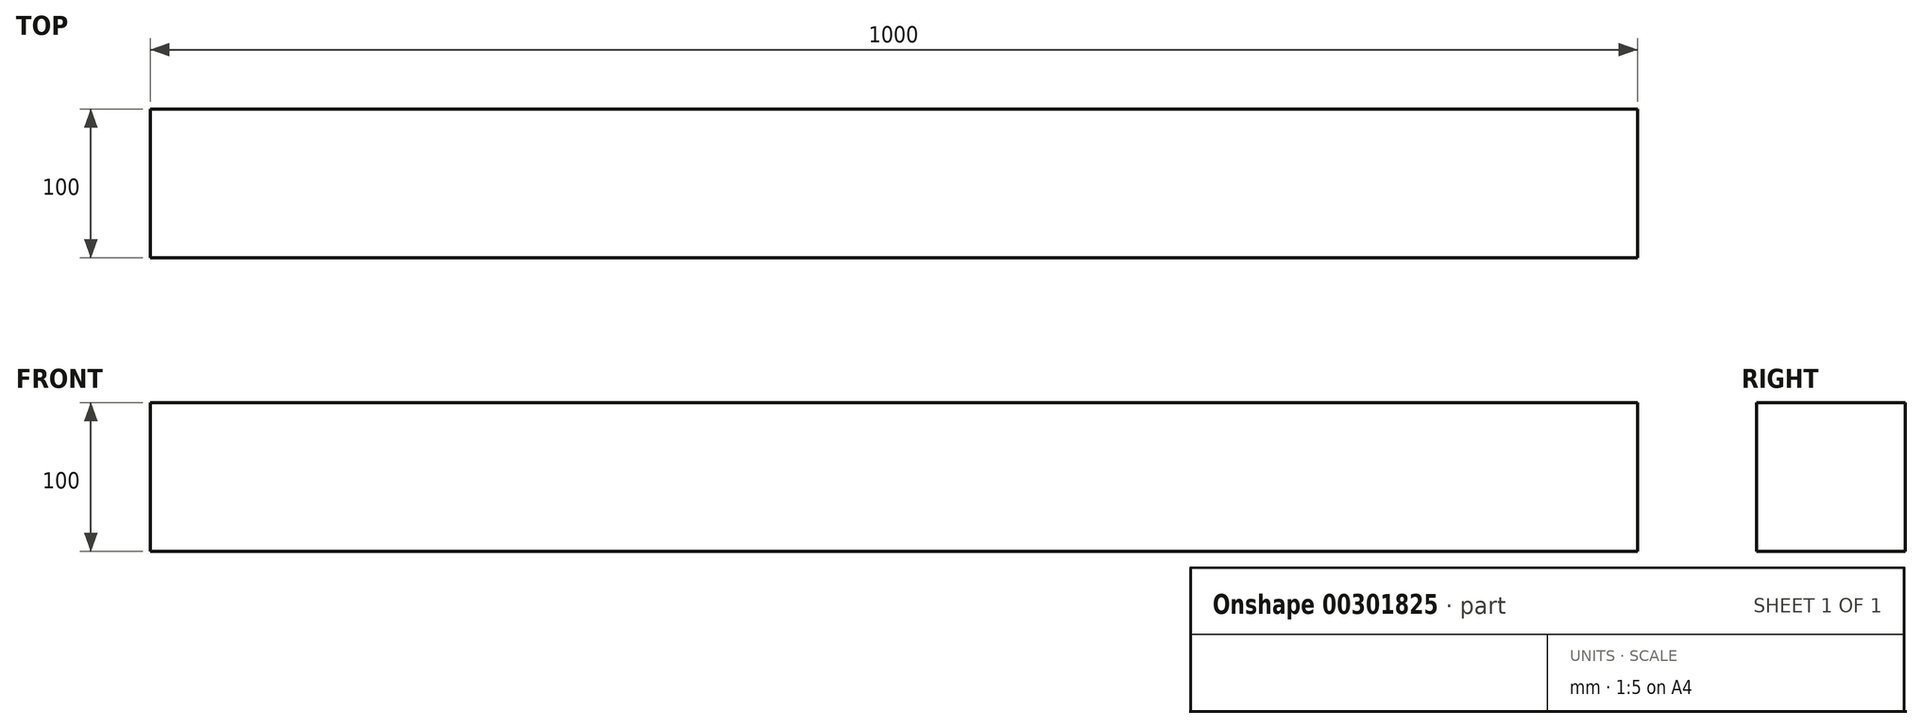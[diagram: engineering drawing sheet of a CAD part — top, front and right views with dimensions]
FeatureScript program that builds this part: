
annotation { "Feature Type Name" : "Feature", "Feature Type Description" : "" }
export const myFeature = defineFeature(function(context is Context, id is Id, definition is map)
    precondition{}
    {
        {
            var Q0;
            Q0=qCreatedBy(makeId("Front.planeOp"),FACE);
            var sketch = newSketch(context, id + "F0", { "sketchPlane" : qUnion([Q0])});
            skLineSegment(sketch, "E0.bottom", {"start": v(500, -50) * mm, "end": v(-500, -50) * mm});
            skLineSegment(sketch, "E0.top", {"start": v(500, 50) * mm, "end": v(-500, 50) * mm});
            skLineSegment(sketch, "E0.left", {"start": v(500, -50) * mm, "end": v(500, 50) * mm});
            skLineSegment(sketch, "E0.right", {"start": v(-500, -50) * mm, "end": v(-500, 50) * mm});
            skPoint(sketch, "E0.middle", {"position": v(0, 0) * mm});
            skSolve(sketch);
        }
        {
            var Q0;
            Q0=qSketchRegion(id+"F0",true);
            extrude(context, id + "F1", {"entities" : qUnion([Q0]), "depth" : 100 * mm});
        }
    });
